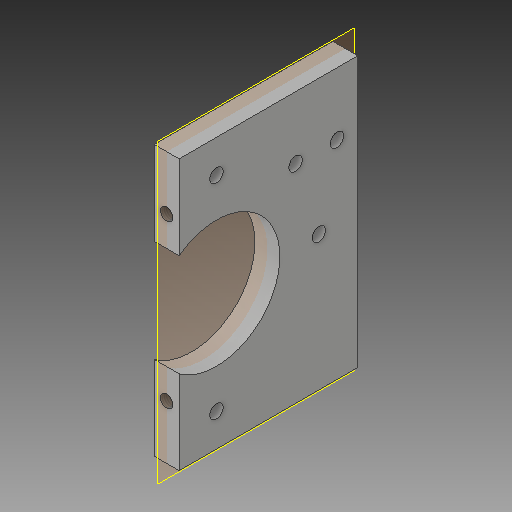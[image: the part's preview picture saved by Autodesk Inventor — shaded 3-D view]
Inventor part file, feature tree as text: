
AUTODESK INVENTOR PART (.ipt)
format: ipt  version: 2018 (Build 220112000, 112)  size: 158,208 bytes
history: native  units: mm
features: extrude x5, sketch x5, thread x4, reference x2, plane x1
ambient origin geometry x8: Origin, YZ Plane, XZ Plane, XY Plane, X Axis, Y Axis, Z Axis, Center Point
bodies: Solid1 (feature_tree)
feature tree (17):
  extrude  "Extrusion1"  Depth=86.0mm
  extrude  "Extrusion2"  Depth=12.0mm
  plane  "Work Plane1"
  extrude  "Extrusion3"  Depth=98.429mm
  extrude  "Extrusion4"  Depth=6.5mm
  extrude  "Extrusion6"  Depth=10.0mm
  thread  "Thread1"  [1 undecoded]
  thread  "Thread2"  [1 undecoded]
  thread  "Thread3"  [1 undecoded]
  thread  "Thread4"  [1 undecoded]
  sketch  "Sketch1"  dims[d0=130.0mm d1=86.0mm]
  sketch  "Sketch2"  dims[d2=12.0mm d3=0.0mm d4=18.0mm]
  sketch  "Sketch3"  dims[d5=18.0mm d6=98.429mm]
  sketch  "Sketch4"  dims[d7=6.5mm d8=6.5mm]
  sketch  "Sketch6"  dims[d9=6.5mm d10=49.2145mm d11=12.0mm d12=0.0mm d13=61.0mm d14=6.0mm d15=26.0mm d17=8.0mm d19=15.0mm d20=0.0mm d21=6.0mm d22=27.0mm d23=15.0mm d25=15.0mm d26=0.0mm d29=18.0mm d30=10.0mm d31=0.0mm d32=0.25mm d33=0.25mm d34=10.0mm d35=0.0mm d36=10.0mm d37=0.0mm d38=10.0mm d39=0.0mm d40=10.0mm d41=0.0mm]
  reference  "Reference3"
  reference  "Reference4"
note: 4 required parameter values undecoded (feature->parameter linkage not recoverable at this tier; creation-order binding heuristic only, values carry confidence <= 0.55)
